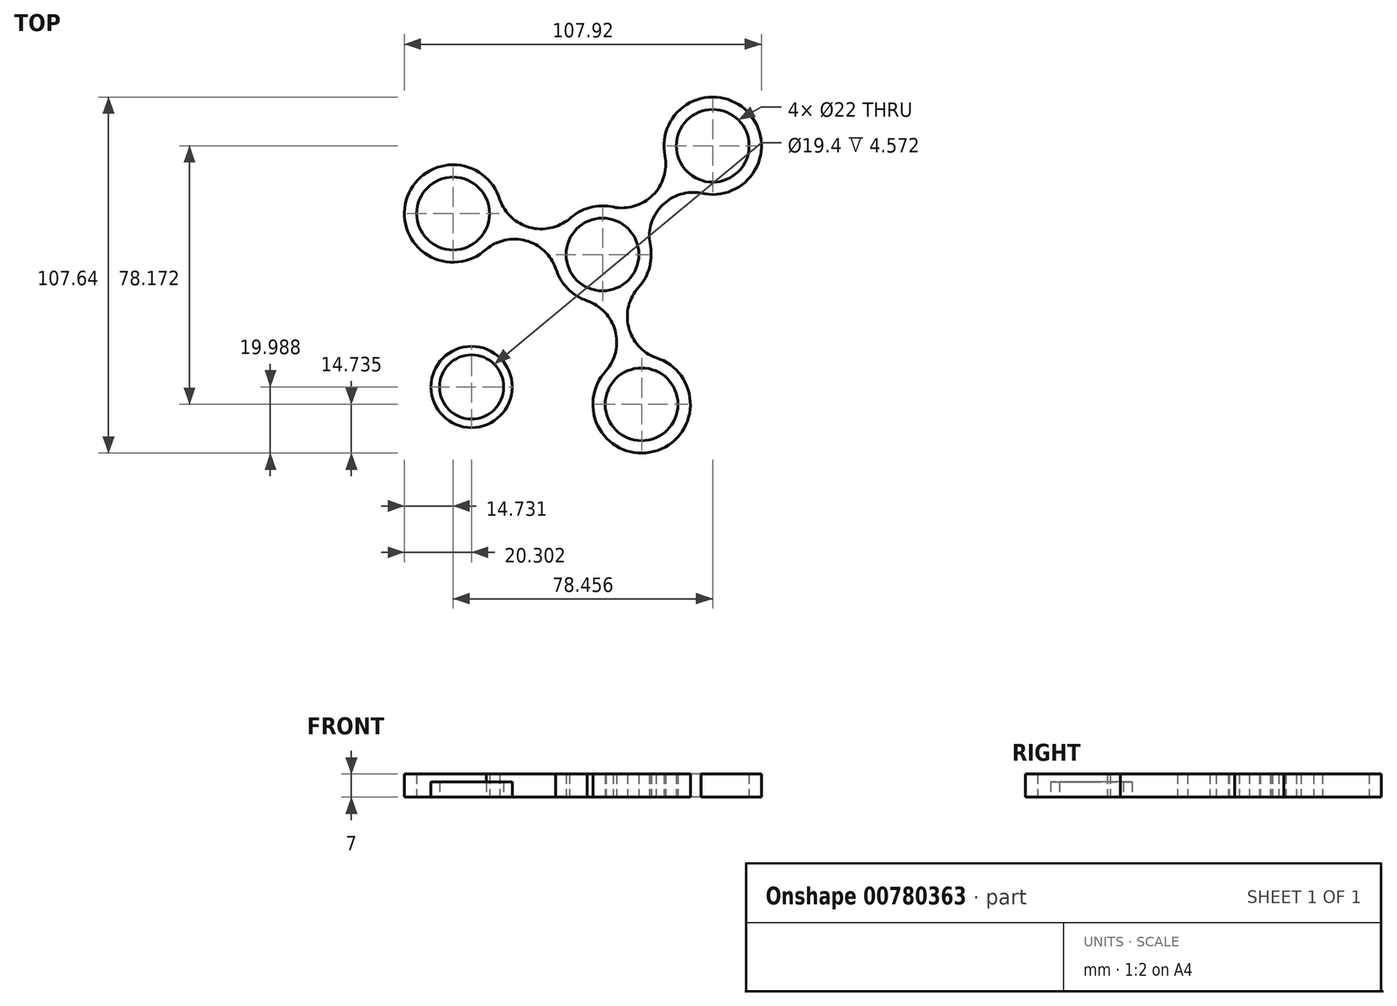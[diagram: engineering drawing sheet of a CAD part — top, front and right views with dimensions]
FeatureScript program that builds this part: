
annotation { "Feature Type Name" : "Feature", "Feature Type Description" : "" }
export const myFeature = defineFeature(function(context is Context, id is Id, definition is map)
    precondition{}
    {
        {
            var Q0;
            Q0=qCreatedBy(makeId("Top.planeOp"),FACE);
            var sketch = newSketch(context, id + "F0", { "sketchPlane" : qUnion([Q0])});
            skCircle(sketch, "E0", {"center": v(0, 0) * mm, "radius": 11 * mm});
            skCircle(sketch, "E1", {"center": v(0, 0) * mm, "radius": 14.73 * mm});
            skCircle(sketch, "E2", {"center": v(-45.14, 12.4) * mm, "radius": 11 * mm});
            skCircle(sketch, "E3", {"center": v(-45.14, 12.4) * mm, "radius": 14.73 * mm});
            skCircle(sketch, "E4", {"center": v(33.32, 32.89) * mm, "radius": 11 * mm});
            skCircle(sketch, "E5", {"center": v(33.32, 32.89) * mm, "radius": 14.73 * mm});
            skCircle(sketch, "E6", {"center": v(11.82, -45.29) * mm, "radius": 11 * mm});
            skCircle(sketch, "E7", {"center": v(11.82, -45.29) * mm, "radius": 14.73 * mm});
            skLineSegment(sketch, "E8", {"start": v(-45.14, 12.4) * mm, "end": v(0, 0) * mm});
            skLineSegment(sketch, "E9", {"start": v(0, 0) * mm, "end": v(33.32, 32.89) * mm});
            skLineSegment(sketch, "E10", {"start": v(0, 0) * mm, "end": v(11.82, -45.3) * mm});
            skPoint(sketch, "E11", {"position": v(-22.57, 6.2) * mm});
            skPoint(sketch, "E12", {"position": v(16.66, 16.44) * mm});
            skPoint(sketch, "E13", {"position": v(5.91, -22.65) * mm});
            skArc(sketch, "E14", {"start": v(-9.43, 11.32) * mm, "mid": v(-21.64, 8.12) * mm, "end": v(-31, 16.57) * mm});
            skArc(sketch, "E15", {"start": v(-35.68, 1.12) * mm, "mid": v(-23.12, 4.2) * mm, "end": v(-13.9, -4.87) * mm});
            skArc(sketch, "E16", {"start": v(2.94, 14.43) * mm, "mid": v(15.08, 17.83) * mm, "end": v(18.9, 29.85) * mm});
            skArc(sketch, "E17", {"start": v(14.35, 3.32) * mm, "mid": v(18.12, 14.96) * mm, "end": v(29.8, 18.58) * mm});
            skArc(sketch, "E18", {"start": v(-4.84, -13.92) * mm, "mid": v(3.82, -22.94) * mm, "end": v(1.12, -35.16) * mm});
            skArc(sketch, "E19", {"start": v(10.9, -9.9) * mm, "mid": v(8, -22.33) * mm, "end": v(16.9, -31.46) * mm});
            skSolve(sketch);
        }
        {
            var Q0;
            Q0=qCreatedBy(makeId("Front.planeOp"),FACE);
            var sketch = newSketch(context, id + "F1", { "sketchPlane" : qUnion([Q0])});
            skLineSegment(sketch, "E20", {"start": v(-0.62, 0) * mm, "end": v(-0.62, 7) * mm});
            skLineSegment(sketch, "E21", {"start": v(-0.62, 7) * mm, "end": v(-0.62, 0) * mm});
            skSolve(sketch);
        }
        {
            var Q0;
            Q0 = qSketchRegion(id + "F1", true);
            var Q1;
            Q1 = qSketchRegion(id + "F0", true);
            extrude(context, id + "F2", {"entities" : qUnion([Q0, Q1]), "depth" : 7 * mm, "offsetDistance" : 25.4 * mm});
        }
        {
            var Q0;
            Q0=qCreatedBy(makeId("Top.planeOp"),FACE);
            var sketch = newSketch(context, id + "F3", { "sketchPlane" : qUnion([Q0])});
            skPoint(sketch, "E22", {"position": v(-39.57, -40.03) * mm});
            skCircle(sketch, "E23", {"center": v(-39.57, -40.03) * mm, "radius": 9.7 * mm});
            skLineSegment(sketch, "E24", {"start": v(-29.87, -40.35) * mm, "end": v(-27.29, -40.35) * mm});
            skCircle(sketch, "E25", {"center": v(-39.57, -40.03) * mm, "radius": 12.29 * mm});
            skSolve(sketch);
        }
        {
            var Q0;
            Q0=makeQuery(id+"F3.imprint","IMPRINT",FACE,{"disambiguationData":[TD([[makeQuery(id+"F3.imprint","IMPRINT",EDGE,{"derivedFrom":sQuery(id+"F3.wireOp",EDGE,"E23")}),-1.0]])]});
            extrude(context, id + "F4", {"entities" : qUnion([Q0]), "depth" : 4.57 * mm, "offsetDistance" : 25.4 * mm});
        }
    });
